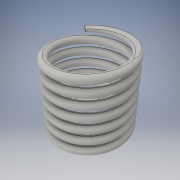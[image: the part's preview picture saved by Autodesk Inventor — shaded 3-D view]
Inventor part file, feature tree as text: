
AUTODESK INVENTOR PART (.ipt)
format: ipt  version: 2016 (Build 200138000, 138)  size: 371,200 bytes
history: native  units: in
note: dims shown in document units (in); Inventor stores cm internally (conversion verified against a paired STEP export)
features: sketch x2, extrude x1, helix x1, projected_geometry x1
ambient origin geometry x8: Origin, YZ Plane, XZ Plane, XY Plane, X Axis, Y Axis, Z Axis, Center Point
bodies: Body1 (feature_tree)
feature tree (5):
  extrude  "Extrusion5"  Depth=19.685in TaperAngle=0.0deg
  helix  "Coil3"  [1 undecoded]
  sketch  "Sketch13"  dims[d28=19.685in d29=19.685in d30=0.0in d31=1.9685in]
  sketch  "Sketch14"  dims[d32=2.7559in d33=19.685in d34=0.3937in d35=0.0in d36=90.0deg d37=90.0deg d38=0.0in d39=0.0in]
  projected_geometry  "Project Cut Edges3"
note: 1 required parameter value undecoded (feature->parameter linkage not recoverable at this tier; creation-order binding heuristic only, values carry confidence <= 0.55)
